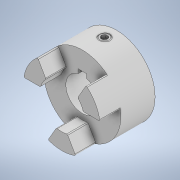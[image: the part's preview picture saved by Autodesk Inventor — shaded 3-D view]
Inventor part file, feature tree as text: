
AUTODESK INVENTOR PART (.ipt)
format: ipt  version: 2021 (Build 250183000, 183)  size: 195,584 bytes
history: native  units: in
note: dims shown in document units (in); Inventor stores cm internally (conversion verified against a paired STEP export)
features: other x1, chamfer x1
ambient origin geometry x8: Origin, YZ Plane, XZ Plane, XY Plane, X Axis, Y Axis, Z Axis, Center Point
bodies: Solid1 (feature_tree), Solid2 (feature_tree)
feature tree (2):
  other  "Cut-Extrude2"
  chamfer  "Chamfer4"  [1 undecoded]
note: 1 required parameter value undecoded (feature->parameter linkage not recoverable at this tier; creation-order binding heuristic only, values carry confidence <= 0.55)
